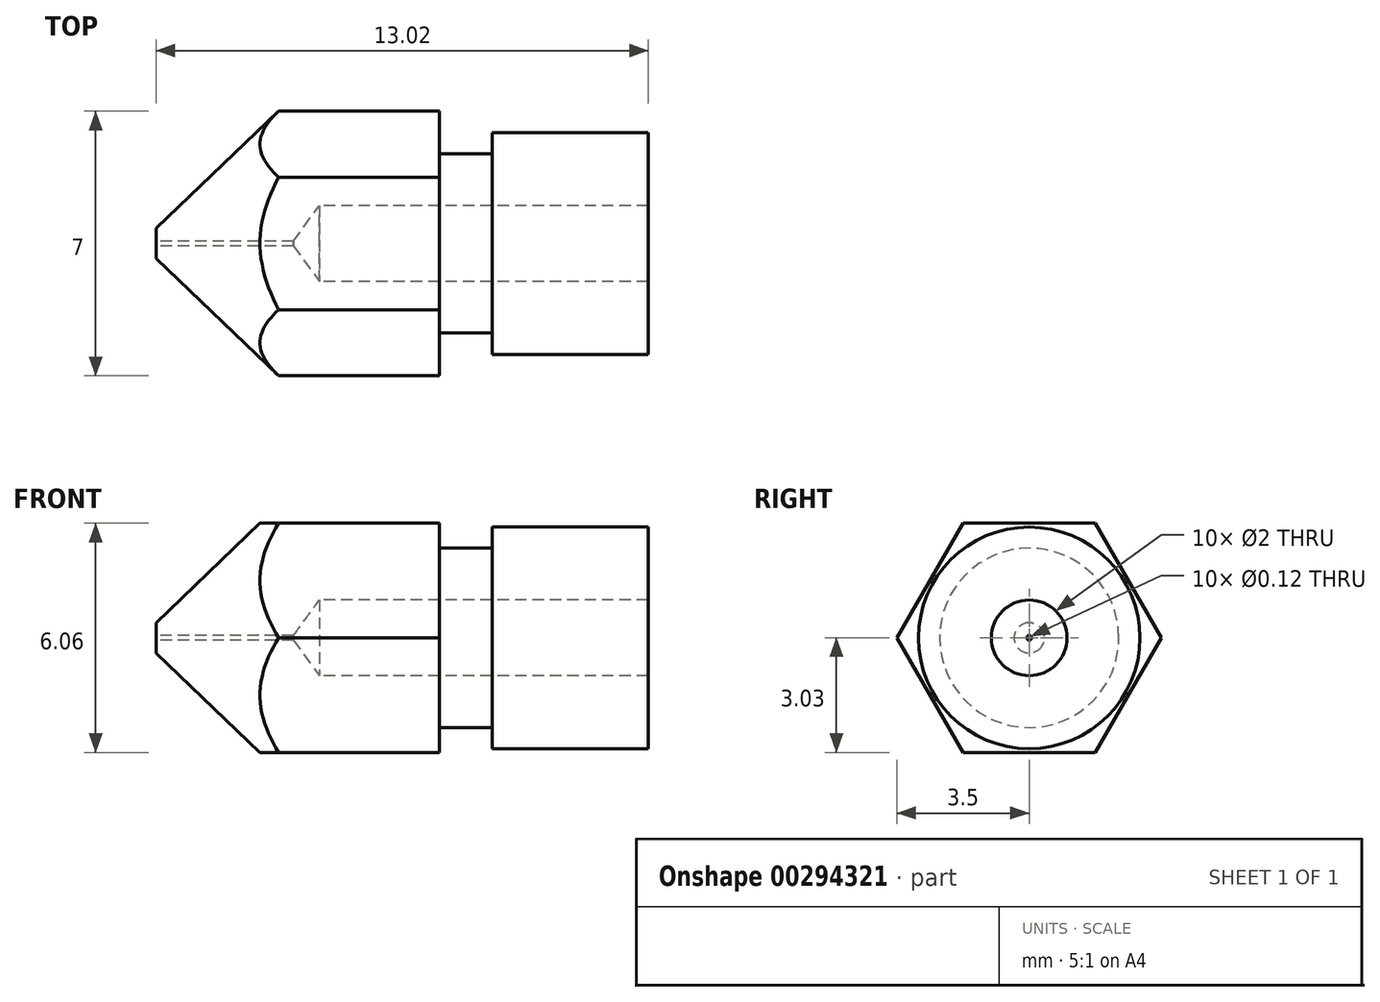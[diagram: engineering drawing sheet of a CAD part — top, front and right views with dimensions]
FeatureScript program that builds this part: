
annotation { "Feature Type Name" : "Feature", "Feature Type Description" : "" }
export const myFeature = defineFeature(function(context is Context, id is Id, definition is map)
    precondition{}
    {
        {
            var Q0;
            Q0=qCreatedBy(makeId("Front.planeOp"),FACE);
            var sketch = newSketch(context, id + "F0", { "sketchPlane" : qUnion([Q0])});
            skLineSegment(sketch, "E0", {"start": v(6.16, 1) * mm, "end": v(-2.55, 1) * mm});
            skLineSegment(sketch, "E1", {"start": v(-2.55, 1) * mm, "end": v(-3.23, 0.06) * mm});
            skLineSegment(sketch, "E2", {"start": v(-3.23, 0.06) * mm, "end": v(-6.86, 0.06) * mm});
            skLineSegment(sketch, "E3", {"start": v(-6.86, 0.06) * mm, "end": v(-6.86, 0.4) * mm});
            skLineSegment(sketch, "E4", {"start": v(-6.86, 0.4) * mm, "end": v(-3.62, 3.5) * mm});
            skLineSegment(sketch, "E5", {"start": v(-3.62, 3.5) * mm, "end": v(0.63, 3.5) * mm});
            skLineSegment(sketch, "E6", {"start": v(0.63, 3.5) * mm, "end": v(0.63, 2.37) * mm});
            skLineSegment(sketch, "E7", {"start": v(0.63, 2.37) * mm, "end": v(2.03, 2.37) * mm});
            skLineSegment(sketch, "E8", {"start": v(2.03, 2.37) * mm, "end": v(2.03, 2.93) * mm});
            skLineSegment(sketch, "E9", {"start": v(2.03, 2.93) * mm, "end": v(6.16, 2.93) * mm});
            skLineSegment(sketch, "E10", {"start": v(6.16, 2.93) * mm, "end": v(6.16, 1) * mm});
            skLineSegment(sketch, "E11", {"start": v(-11.06, 0) * mm, "end": v(6.87, 0) * mm, "construction": true});
            skSolve(sketch);
        }
        {
            var Q0;
            Q0 = qSketchRegion(id + "F0", true);
            var Q1;
            Q1=sQuery(id+"F0.wireOp",EDGE,"E11");
            revolve(context, id + "F1", {"entities" : qUnion([Q0]), "axis" : qUnion([Q1]), "revolveType" : RevolveType.FULL});
        }
        {
            var Q0;
            Q0=makeQuery(id+"F1.opRevolve","SWEPT_FACE",FACE,{"disambiguationData":[OSD([sQuery(id+"F0.wireOp",EDGE,"E6")])]});
            var sketch = newSketch(context, id + "F2", { "sketchPlane" : qUnion([Q0])});
            skCircle(sketch, "E12.cCircle", {"center": v(0, 0) * mm, "radius": 3.03 * mm, "construction": true});
            skLineSegment(sketch, "E12.0", {"start": v(-1.75, 3.03) * mm, "end": v(1.75, 3.03) * mm});
            skLineSegment(sketch, "E12.1", {"start": v(1.75, 3.03) * mm, "end": v(3.5, 0) * mm});
            skLineSegment(sketch, "E12.2", {"start": v(3.5, 0) * mm, "end": v(1.75, -3.03) * mm});
            skLineSegment(sketch, "E12.3", {"start": v(1.75, -3.03) * mm, "end": v(-1.75, -3.03) * mm});
            skLineSegment(sketch, "E12.4", {"start": v(-1.75, -3.03) * mm, "end": v(-3.5, 0) * mm});
            skLineSegment(sketch, "E12.5", {"start": v(-3.5, 0) * mm, "end": v(-1.75, 3.03) * mm});
            skPoint(sketch, "E12.0.midPoint", {"position": v(0, 3.03) * mm});
            skSolve(sketch);
        }
        {
            var Q0;
            Q0 = qSketchRegion(id + "F2", true);
            extrude(context, id + "F3", {"entities" : qUnion([Q0]), "operationType" : NewBodyOperationType.INTERSECT, "endBound" : BoundingType.SYMMETRIC, "oppositeDirection" : true, "depth" : 25 * mm});
        }
    });
